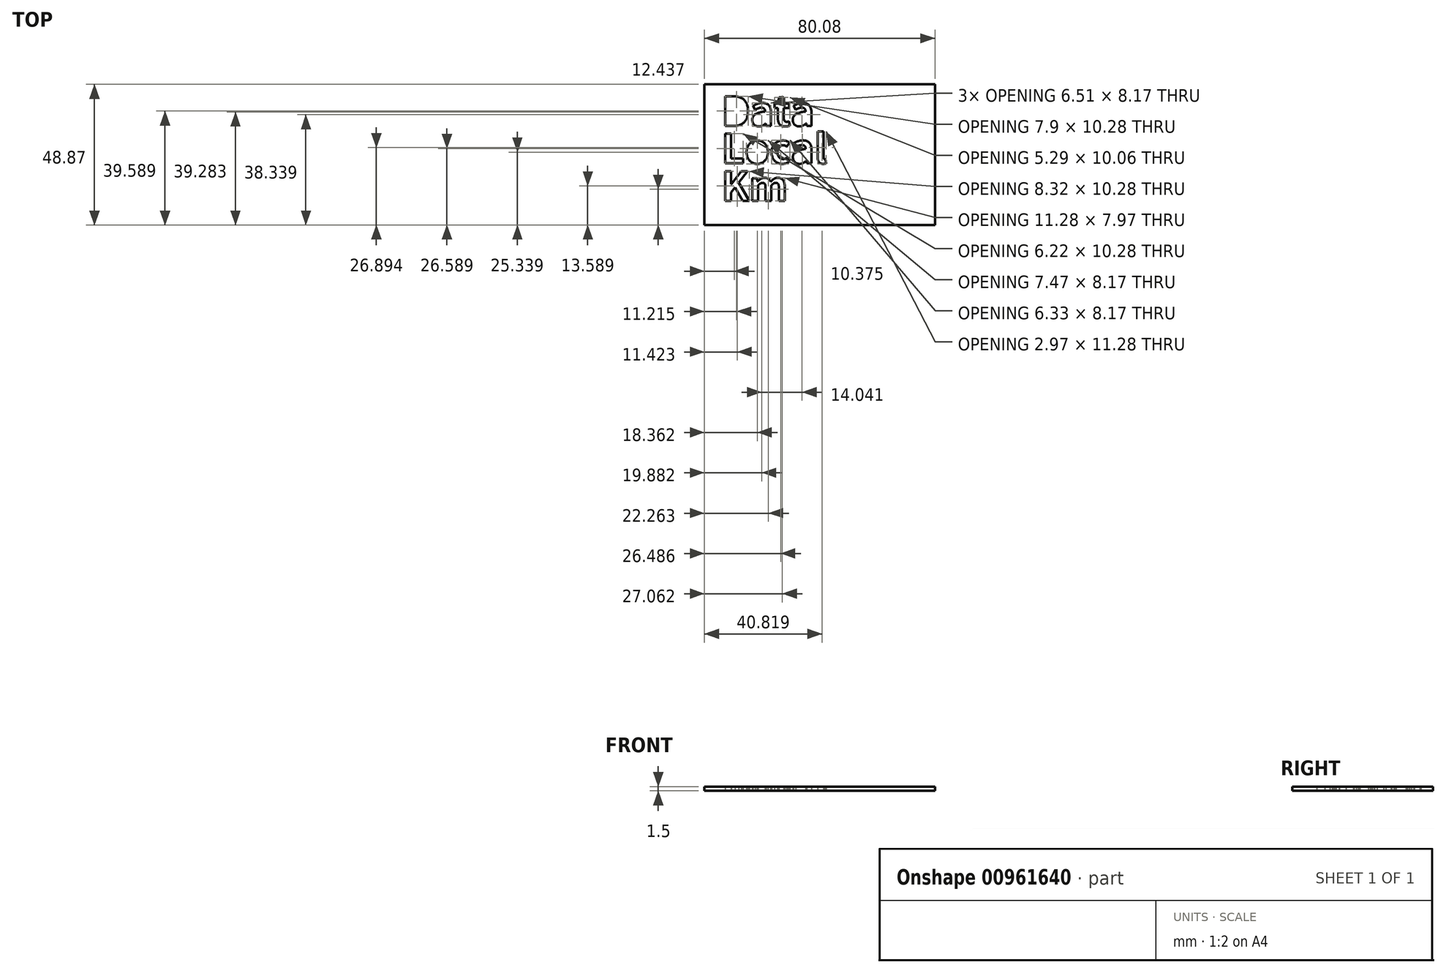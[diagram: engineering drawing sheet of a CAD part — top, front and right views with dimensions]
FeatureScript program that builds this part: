
annotation { "Feature Type Name" : "Feature", "Feature Type Description" : "" }
export const myFeature = defineFeature(function(context is Context, id is Id, definition is map)
    precondition{}
    {
        {
            var Q0;
            Q0=qCreatedBy(makeId("Top.planeOp"),FACE);
            var sketch = newSketch(context, id + "F0", { "sketchPlane" : qUnion([Q0])});
            skLineSegment(sketch, "E0.bottom", {"start": v(50, 30) * mm, "end": v(-50, 30) * mm});
            skLineSegment(sketch, "E0.top", {"start": v(50, -30) * mm, "end": v(-50, -30) * mm});
            skLineSegment(sketch, "E0.left", {"start": v(50, 30) * mm, "end": v(50, -30) * mm});
            skLineSegment(sketch, "E0.right", {"start": v(-50, 30) * mm, "end": v(-50, -30) * mm});
            skPoint(sketch, "E0.middle", {"position": v(0, 0) * mm});
            skText(sketch, "E1", { "text": "Data", "fontName": "NotoSansCJKjp-Bold.otf"});
            skLineSegment(sketch, "E2", {"start": v(-44, 15.58) * mm, "end": v(-44, -0.42) * mm});
            skText(sketch, "E3", { "text": "Km", "fontName": "NotoSansCJKjp-Bold.otf"});
            skLineSegment(sketch, "E4", {"start": v(-44, -0.42) * mm, "end": v(-44, -10.42) * mm});
            skLineSegment(sketch, "E5", {"start": v(-44, 15.58) * mm, "end": v(-44, 12.58) * mm});
            skText(sketch, "E6", { "text": "Local", "fontName": "NotoSansCJKjp-Bold.otf"});
            skLineSegment(sketch, "E7", {"start": v(-50, -18.87) * mm, "end": v(50, -18.87) * mm});
            skLineSegment(sketch, "E8", {"start": v(50, -18.87) * mm, "end": v(30.08, -18.87) * mm});
            skLineSegment(sketch, "E9", {"start": v(30.08, -18.87) * mm, "end": v(30.08, 30) * mm});
            const initialGuessF0  = {"E1": [-0.044, 0.01558, 1, 0, 0.01], "E3": [-0.044, -0.01042, 1, 0, 0.01], "E6": [-0.044, 0.00258, 1, 0, 0.01]};
            skSetInitialGuess(sketch, initialGuessF0);
            skSolve(sketch);
        }
        {
            var Q0;
            Q0=makeQuery(id+"F0.imprint","IMPRINT",FACE,{"disambiguationData":[TD([[makeQuery(id+"F0.imprint","IMPRINT",EDGE,{"derivedFrom":sQuery(id+"F0.wireOp",EDGE,"E1.sketch_text.stroke-0")}),-1.0]])]});
            extrude(context, id + "F1", {"entities" : qUnion([Q0]), "depth" : 1.5 * mm, "offsetDistance" : 25 * mm});
        }
    });
